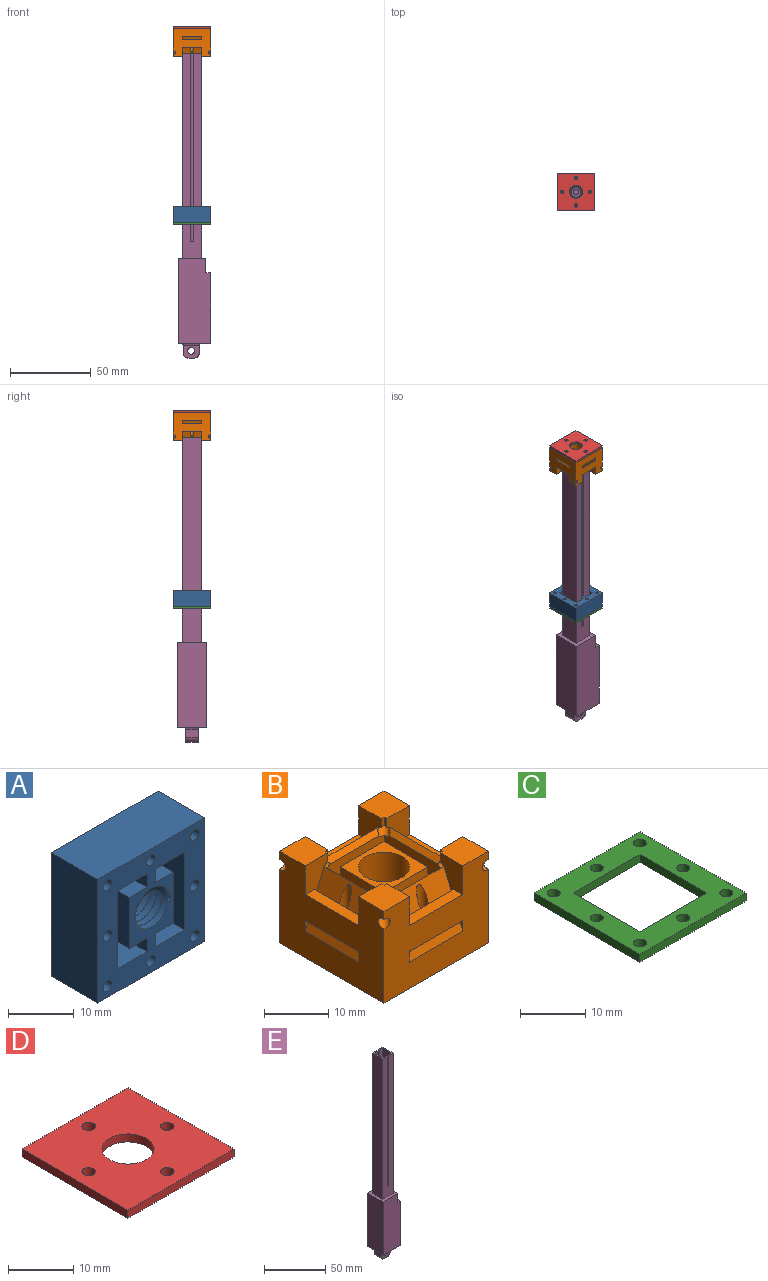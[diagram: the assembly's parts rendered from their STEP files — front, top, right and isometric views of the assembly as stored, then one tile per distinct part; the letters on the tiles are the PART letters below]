
ASSEMBLY  parts=5 mates=9
PART A: 38 faces, bbox 23.6x11.5x23.6 mm
  f0: cylinder r=0.95mm len=10mm, axis (0,-1,0), area 59.7mm2, adj f20,f21
  f1: cylinder r=0.95mm len=10mm, axis (0,-1,0), area 59.7mm2, adj f20,f21
  f2: cylinder r=0.95mm len=10mm, axis (0,-1,0), area 59.7mm2, adj f20,f21
  f3: cylinder r=0.95mm len=10mm, axis (0,-1,0), area 59.7mm2, adj f20,f21
  f4: cylinder r=0.95mm len=10mm, axis (0,-1,0), area 59.7mm2, adj f20,f21
  f5: cylinder r=0.95mm len=10mm, axis (0,-1,0), area 59.7mm2, adj f20,f21
  f6: plane 10x2.5mm, normal (1,0,0), area 25mm2, adj f18,f20,f21,f32
  f7: plane 10x2.5mm, normal (-1,0,0), area 25mm2, adj f9,f20,f21,f26
  f8: plane 10x3.85mm, normal (0,0,-1), area 38.5mm2, adj f19,f20,f21,f25
  f9: plane 10x3.85mm, normal (0,0,1), area 38.5mm2, adj f7,f19,f20,f21
  f10: plane 0.54x0.26mm, normal (0,0,1), area 0.1mm2, adj f14,f15,f20,f23
  f11: bspline ~9.47x9.17mm, area 18.6mm2, adj f12,f15,f20,f22
  f12: bspline ~10.3x9.24mm, area 170.5mm2, adj f11,f13,f20,f22
  f13: cylinder r=3.12mm len=9.75mm, axis (0,1,0), area 16.6mm2, adj f12,f14,f20,f22
  f14: bspline ~10.51x9.25mm, area 181.5mm2, adj f10,f13,f20,f21,f22,f23
  f15: cylinder r=4.1mm len=10mm, axis (0,-1,0), area 34.7mm2, adj f10,f11,f20,f21,f22,f23
  f16: plane 10x3.85mm, normal (0,0,-1), area 38.5mm2, adj f17,f20,f21,f24
  f17: plane 10x9.5mm, normal (1,0,0), area 95mm2, adj f16,f18,f20,f21
  f18: plane 10x3.85mm, normal (0,0,1), area 38.5mm2, adj f6,f17,f20,f21
  f19: plane 10x9.5mm, normal (-1,0,0), area 95mm2, adj f8,f9,f20,f21
  f20: plane 23.59x23.59mm, normal (0,-1,0), area 353.4mm2, adj f0,f1,f2,f3,f4,f5,f6,f7
  f21: plane 23.14x23.14mm, normal (0,1,0), area 344.1mm2, adj f0,f1,f2,f3,f4,f5,f6,f7
  f22: plane 0.98x0.88mm, normal (0,0,-1), area 0.6mm2, adj f11,f12,f13,f14,f15,f21
  f23: bspline ~9.79x9.47mm, area 18.6mm2, adj f10,f14,f15,f21
  f24: plane 10x2.5mm, normal (1,0,0), area 25mm2, adj f16,f20,f21,f27
  f25: plane 10x2.5mm, normal (-1,0,0), area 25mm2, adj f8,f20,f21,f34
  f26: plane 10x6.35mm, normal (0,0,-1), area 63.5mm2, adj f7,f20,f21,f33
  f27: plane 10x6.35mm, normal (0,0,1), area 63.5mm2, adj f20,f21,f24,f31
  f28: plane 23x10mm, normal (0,0,-1), area 230mm2, adj f20,f21,f29,f35
  f29: plane 23x10mm, normal (-1,0,0), area 230mm2, adj f20,f21,f28,f30
  f30: plane 23x10mm, normal (0,0,1), area 230mm2, adj f20,f21,f29,f35
  f31: plane 14.5x10mm, normal (-1,0,0), area 145mm2, adj f20,f21,f27,f32
  f32: plane 10x6.35mm, normal (0,0,-1), area 63.5mm2, adj f6,f20,f21,f31
  f33: plane 14.5x10mm, normal (1,0,0), area 145mm2, adj f20,f21,f26,f34
  f34: plane 10x6.35mm, normal (0,0,1), area 63.5mm2, adj f20,f21,f25,f33
  f35: plane 23x10mm, normal (1,0,0), area 230mm2, adj f20,f21,f28,f30
  f36: cylinder r=0.95mm len=10mm, axis (0,-1,0), area 59.7mm2, adj f20,f21
  f37: cylinder r=0.95mm len=10mm, axis (0,-1,0), area 59.7mm2, adj f20,f21
PART B: 60 faces, bbox 25.3x25.3x18.5 mm
  f0: plane 13x13mm, normal (0,0,1), area 74.9mm2, adj f1,f2,f6,f18,f56,f57,f58,f59
  f1: plane 13.12x12.12mm, normal (1,0,0), area 155.3mm2, adj f0,f2,f18,f27,f39,f51
  f2: plane 13.12x12.12mm, normal (0,-1,0), area 155.3mm2, adj f0,f1,f6,f31,f43,f51
  f3: plane 5.6x5.6mm, normal (0,0,1), area 31mm2, adj f5,f10,f13,f15,f26,f49
  f4: plane 1.66x0.61mm, normal (0,1,0), area 0.9mm2, adj f8,f21,f27,f47
  f5: plane 1.66x0.61mm, normal (0,1,0), area 0.9mm2, adj f3,f10,f35,f49
  f6: plane 13.12x12.12mm, normal (-1,0,0), area 155.3mm2, adj f0,f2,f18,f23,f35,f43
  f7: plane 1.66x0.61mm, normal (0,-1,0), area 0.9mm2, adj f14,f19,f34,f43
  f8: plane 5.6x5.6mm, normal (0,0,1), area 31mm2, adj f4,f15,f16,f21,f40,f47
  f9: plane 1.66x0.61mm, normal (1,0,0), area 0.9mm2, adj f11,f20,f42,f51
  f10: plane 1.66x0.61mm, normal (-1,0,0), area 0.9mm2, adj f3,f5,f26,f35
  f11: plane 5.6x5.6mm, normal (0,0,1), area 31mm2, adj f9,f12,f16,f20,f33,f42
  f12: plane 23x17.5mm, normal (0,1,0), area 310mm2, adj f11,f13,f14,f16,f17,f32,f33,f34
  f13: plane 23x17.5mm, normal (1,0,0), area 310mm2, adj f3,f12,f14,f15,f17,f24,f25,f26
  f14: plane 5.6x5.6mm, normal (0,0,1), area 31mm2, adj f7,f12,f13,f19,f25,f34
  f15: plane 23x17.5mm, normal (0,-1,0), area 310mm2, adj f3,f8,f13,f16,f17,f27,f35,f47
  f16: plane 23x17.5mm, normal (-1,0,0), area 310mm2, adj f8,f11,f12,f15,f17,f27,f40,f41
  f17: plane 23x23mm, normal (0,0,-1), area 467.4mm2, adj f12,f13,f15,f16,f22,f30,f38,f46
  f18: plane 13.12x12.12mm, normal (0,1,0), area 155.3mm2, adj f0,f1,f6,f27,f35,f48
  f19: plane 1.66x0.61mm, normal (-1,0,0), area 0.9mm2, adj f7,f14,f25,f43
  f20: plane 1.66x0.61mm, normal (0,-1,0), area 0.9mm2, adj f9,f11,f33,f51
  f21: plane 1.66x0.61mm, normal (1,0,0), area 0.9mm2, adj f4,f8,f27,f40
  f22: cylinder r=4mm len=14.5mm, axis (0,0,-1), area 364.4mm2, adj f17,f55
  f23: plane 11.97x1.03mm, normal (-0.71,0,0.71), area 13.6mm2, adj f6,f24,f25,f26,f35,f43
  f24: plane 12.8x11.36mm, normal (0.93,0,0.37), area 124mm2, adj f13,f23,f25,f26,f30
  f25: plane 12.64x5.14mm, normal (0,-1,0), area 27mm2, adj f13,f14,f19,f23,f24,f28,f29,f43
  f26: plane 12.64x5.14mm, normal (0,1,0), area 27mm2, adj f3,f10,f13,f23,f24,f28,f29,f35
  f27: cylinder r=0.95mm len=6.91mm, axis (0.71,0.71,0), area 40.4mm2, adj f1,f4,f15,f16,f18,f21,f39,f40
  f28: plane 11.8x5mm, normal (-0.93,0,-0.37), area 63.5mm2, adj f13,f25,f26,f29
  f29: plane 11.8x2mm, normal (0,0,1), area 23.6mm2, adj f13,f25,f26,f28
  f30: cylinder r=0.95mm len=14.88mm, axis (0,0,-1), area 74.6mm2, adj f17,f24
  f31: plane 11.97x1.03mm, normal (0,-0.71,0.71), area 13.6mm2, adj f2,f32,f33,f34,f43,f51
  f32: plane 12.8x11.36mm, normal (0,0.93,0.37), area 124mm2, adj f12,f31,f33,f34,f38
  f33: plane 12.64x5.14mm, normal (1,0,0), area 27mm2, adj f11,f12,f20,f31,f32,f36,f37,f51
  f34: plane 12.64x5.14mm, normal (-1,0,0), area 27mm2, adj f7,f12,f14,f31,f32,f36,f37,f43
  f35: cylinder r=0.95mm len=6.91mm, axis (-0.71,0.71,0), area 40.4mm2, adj f5,f6,f10,f13,f15,f18,f23,f26
  f36: plane 11.8x5mm, normal (0,-0.93,-0.37), area 63.5mm2, adj f12,f33,f34,f37
  f37: plane 11.8x2mm, normal (0,0,1), area 23.6mm2, adj f12,f33,f34,f36
  f38: cylinder r=0.95mm len=14.88mm, axis (0,0,-1), area 74.6mm2, adj f17,f32
  f39: plane 11.97x1.03mm, normal (0.71,0,0.71), area 13.6mm2, adj f1,f27,f40,f41,f42,f51
  f40: plane 12.64x5.14mm, normal (0,1,0), area 27mm2, adj f8,f16,f21,f27,f39,f41,f44,f45
  f41: plane 11.8x10.36mm, normal (-0.93,0,0.37), area 124mm2, adj f16,f39,f40,f42,f46
  f42: plane 12.64x5.14mm, normal (0,-1,0), area 27mm2, adj f9,f11,f16,f39,f41,f44,f45,f51
  f43: cylinder r=0.95mm len=6.91mm, axis (-0.71,-0.71,0), area 40.4mm2, adj f2,f6,f7,f12,f13,f19,f23,f25
  f44: plane 11.8x5mm, normal (0.93,0,-0.37), area 63.5mm2, adj f16,f40,f42,f45
  f45: plane 11.8x2mm, normal (0,0,1), area 23.6mm2, adj f16,f40,f42,f44
  f46: cylinder r=0.95mm len=14.91mm, axis (0,0,-1), area 74.6mm2, adj f17,f41
  f47: plane 12.64x5.14mm, normal (1,0,0), area 27mm2, adj f4,f8,f15,f27,f48,f50,f52,f53
  f48: plane 11.97x1.03mm, normal (0,0.71,0.71), area 13.6mm2, adj f18,f27,f35,f47,f49,f50
  f49: plane 12.64x5.14mm, normal (-1,0,0), area 27mm2, adj f3,f5,f15,f35,f48,f50,f52,f53
  f50: plane 12.8x11.36mm, normal (0,-0.93,0.37), area 124mm2, adj f15,f47,f48,f49,f54
  f51: cylinder r=0.95mm len=6.91mm, axis (0.71,-0.71,0), area 40.4mm2, adj f1,f2,f9,f12,f16,f20,f31,f33
  f52: plane 11.8x5mm, normal (0,0.93,-0.37), area 63.5mm2, adj f15,f47,f49,f53
  f53: plane 11.8x2mm, normal (0,0,1), area 23.6mm2, adj f15,f47,f49,f52
  f54: cylinder r=0.95mm len=14.88mm, axis (0,0,-1), area 74.6mm2, adj f17,f50
  f55: plane 9.7x9.7mm, normal (0,0,1), area 43.8mm2, adj f22,f56,f57,f58,f59
  f56: plane 12x9.7mm, normal (0,-1,0), area 116.4mm2, adj f0,f55,f57,f58
  f57: plane 12x9.7mm, normal (1,0,0), area 116.4mm2, adj f0,f55,f56,f59
  f58: plane 12x9.7mm, normal (-1,0,0), area 116.4mm2, adj f0,f55,f56,f59
  f59: plane 12x9.7mm, normal (0,1,0), area 116.4mm2, adj f0,f55,f57,f58
PART C: 18 faces, bbox 23x23x1.5 mm
  f0: plane 23x1.5mm, normal (0,-1,0), area 34.5mm2, adj f1,f15,f16,f17
  f1: plane 23x1.5mm, normal (1,0,0), area 34.5mm2, adj f0,f2,f16,f17
  f2: plane 23x1.5mm, normal (0,1,0), area 34.5mm2, adj f1,f15,f16,f17
  f3: plane 14.5x1.5mm, normal (-1,0,0), area 21.8mm2, adj f4,f6,f16,f17
  f4: plane 14.5x1.5mm, normal (0,1,0), area 21.8mm2, adj f3,f5,f16,f17
  f5: plane 14.5x1.5mm, normal (1,0,0), area 21.8mm2, adj f4,f6,f16,f17
  f6: plane 14.5x1.5mm, normal (0,-1,0), area 21.8mm2, adj f3,f5,f16,f17
  f7: cylinder r=1mm len=2mm, axis (0,0,-1), area 9.4mm2, adj f16,f17
  f8: cylinder r=1mm len=2mm, axis (0,0,-1), area 9.4mm2, adj f16,f17
  f9: cylinder r=1mm len=2mm, axis (0,0,-1), area 9.4mm2, adj f16,f17
  f10: cylinder r=1mm len=2mm, axis (0,0,-1), area 9.4mm2, adj f16,f17
  f11: cylinder r=1mm len=2mm, axis (0,0,-1), area 9.4mm2, adj f16,f17
  f12: cylinder r=1mm len=2mm, axis (0,0,-1), area 9.4mm2, adj f16,f17
  f13: cylinder r=1mm len=2mm, axis (0,0,-1), area 9.4mm2, adj f16,f17
  f14: cylinder r=1mm len=2mm, axis (0,0,-1), area 9.4mm2, adj f16,f17
  f15: plane 23x1.5mm, normal (-1,0,0), area 34.5mm2, adj f0,f2,f16,f17
  f16: plane 23x23mm, normal (0,0,1), area 293.6mm2, adj f0,f1,f2,f3,f4,f5,f6,f7
  f17: plane 23x23mm, normal (0,0,-1), area 293.6mm2, adj f0,f1,f2,f3,f4,f5,f6,f7
PART D: 11 faces, bbox 23x23x1.5 mm
  f0: plane 23x1.5mm, normal (0,-1,0), area 34.5mm2, adj f1,f8,f9,f10
  f1: plane 23x1.5mm, normal (1,0,0), area 34.5mm2, adj f0,f2,f9,f10
  f2: plane 23x1.5mm, normal (0,1,0), area 34.5mm2, adj f1,f8,f9,f10
  f3: cylinder r=1.05mm len=2.1mm, axis (0,0,-1), area 9.9mm2, adj f9,f10
  f4: cylinder r=1.05mm len=2.1mm, axis (0,0,-1), area 9.9mm2, adj f9,f10
  f5: cylinder r=1.05mm len=2.1mm, axis (0,0,-1), area 9.9mm2, adj f9,f10
  f6: cylinder r=1.05mm len=2.1mm, axis (0,0,-1), area 9.9mm2, adj f9,f10
  f7: cylinder r=4mm len=8mm, axis (0,0,-1), area 37.7mm2, adj f9,f10
  f8: plane 23x1.5mm, normal (-1,0,0), area 34.5mm2, adj f0,f2,f9,f10
  f9: plane 23x23mm, normal (0,0,1), area 464.9mm2, adj f0,f1,f2,f3,f4,f5,f6,f7
  f10: plane 23x23mm, normal (0,0,-1), area 464.9mm2, adj f0,f1,f2,f3,f4,f5,f6,f7
PART E: 39 faces, bbox 20x18x202 mm
  f0: plane 140x12mm, normal (0,-1,0), area 1420mm2, adj f1,f3,f13,f14,f17,f34,f35,f36
  f1: plane 12x5mm, normal (0,0,1), area 20mm2, adj f0,f10,f12,f14,f15,f16,f31,f36
  f2: plane 20x18mm, normal (0,0,-1), area 240mm2, adj f4,f7,f8,f9,f27,f28,f29,f30
  f3: plane 18x17mm, normal (0,0,1), area 162mm2, adj f0,f6,f7,f8,f9,f13,f14,f15
  f4: plane 44x18mm, normal (1,0,0), area 792mm2, adj f2,f5,f8,f9
  f5: plane 18x3mm, normal (0,0,1), area 54mm2, adj f4,f6,f8,f9
  f6: plane 18x9mm, normal (1,0,0), area 162mm2, adj f3,f5,f8,f9
  f7: plane 53x18mm, normal (-1,0,0), area 954mm2, adj f2,f3,f8,f9
  f8: plane 53x20mm, normal (0,-1,0), area 1033mm2, adj f2,f3,f4,f5,f6,f7
  f9: plane 53x20mm, normal (0,1,0), area 1033mm2, adj f2,f3,f4,f5,f6,f7
  f10: plane 140x10mm, normal (0,1,0), area 1140mm2, adj f1,f11,f16,f17,f18,f34,f35,f36
  f11: plane 140x10mm, normal (1,0,0), area 1400mm2, adj f10,f12,f17,f18
  f12: plane 140x10mm, normal (0,-1,0), area 1140mm2, adj f1,f11,f16,f17,f18,f31,f32,f33
  f13: plane 140x12mm, normal (-1,0,0), area 1680mm2, adj f0,f3,f15,f17
  f14: plane 140x12mm, normal (1,0,0), area 1680mm2, adj f0,f1,f3,f15
  f15: plane 140x12mm, normal (0,1,0), area 1420mm2, adj f1,f3,f13,f14,f17,f31,f32,f33
  f16: plane 140x10mm, normal (-1,0,0), area 1400mm2, adj f1,f10,f12,f18
  f17: plane 12x5mm, normal (0,0,1), area 20mm2, adj f0,f10,f11,f12,f13,f15,f33,f34
  f18: plane 10x10mm, normal (0,0,1), area 92.9mm2, adj f10,f11,f12,f16,f37
  f19: plane 8x5mm, normal (-1,0,0), area 40mm2, adj f20,f22,f26,f27
  f20: plane 10x8mm, normal (0,1,0), area 62mm2, adj f19,f21,f23,f24,f25,f26,f28
  f21: plane 8x5mm, normal (1,0,0), area 40mm2, adj f20,f22,f25,f30
  f22: plane 10x8mm, normal (0,-1,0), area 62mm2, adj f19,f21,f23,f24,f25,f26,f29
  f23: plane 8x4mm, normal (0,0,-1), area 32mm2, adj f20,f22,f25,f26
  f24: cylinder r=2.12mm len=8mm, axis (0,-1,0), area 106.8mm2, adj f20,f22
  f25: cylinder r=3mm len=8mm, axis (0,1,0), area 37.7mm2, adj f20,f21,f22,f23
  f26: cylinder r=3mm len=8mm, axis (0,-1,0), area 37.7mm2, adj f19,f20,f22,f23
  f27: cylinder r=1mm len=10mm, axis (0,1,0), area 13.7mm2, adj f2,f19,f28,f29
  f28: cylinder r=1mm len=12mm, axis (1,0,0), area 16.8mm2, adj f2,f20,f27,f30
  f29: cylinder r=1mm len=12mm, axis (-1,0,0), area 16.8mm2, adj f2,f22,f27,f30
  f30: cylinder r=1mm len=10mm, axis (0,-1,0), area 13.7mm2, adj f2,f21,f28,f29
  f31: plane 130x1mm, normal (-1,0,0), area 130mm2, adj f1,f12,f15,f32
  f32: plane 2x1mm, normal (0,0,1), area 2mm2, adj f12,f15,f31,f33
  f33: plane 130x1mm, normal (1,0,0), area 130mm2, adj f12,f15,f17,f32
  f34: plane 130x1mm, normal (1,0,0), area 130mm2, adj f0,f10,f17,f35
  f35: plane 2x1mm, normal (0,0,1), area 2mm2, adj f0,f10,f34,f36
  f36: plane 130x1mm, normal (-1,0,0), area 130mm2, adj f0,f1,f10,f35
  f37: cylinder r=1.5mm len=135mm, axis (0,0,-1), area 1272.3mm2, adj f18,f38
  f38: plane 3x3mm, normal (0,0,1), area 7.1mm2, adj f37
PLACE A rot(axis=(-1,0,0),90deg) t=(-1.5,-9,53.13)mm
PLACE B rot(axis=(1,0,0),180deg) t=(-1.5,-9,173.5)mm
PLACE C t=(-1.5,-9,51.63)mm
PLACE D rot(axis=(1,0,0),180deg) t=(-1.5,-9,175)mm
PLACE E at identity fixed
MATE parallel E.f14 <-> A.f31  axis (1,0,0) through (4.5,-9,101)mm
MATE slider C.f9 <-> A.f3  axis (0,0,-1) through (7.88,-18.38,51.63)mm
MATE parallel E.f15 <-> A.f26  axis (0,1,0) through (4.5,-3,101)mm
MATE planar B.f46 <-> D.f4  axis (0,0,1) through (-10,-9,173.5)mm
MATE planar B.f15 <-> A.f30  axis (0,1,0) through (-7.4,2.5,168.5)mm
MATE planar A.f21 <-> C.f16  axis (0,0,-1) through (-1.48,-8.99,53.13)mm
MATE slider B.f38 <-> D.f3  axis (0,0,1) through (-1.5,-17.5,173.5)mm
MATE planar B.f0 <-> E.f1  axis (0,0,-1) through (3.35,-4.15,171)mm
MATE planar A.f35 <-> B.f13  axis (1,0,0) through (10,-9,58.13)mm
